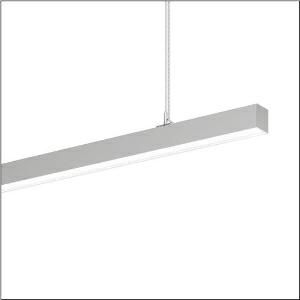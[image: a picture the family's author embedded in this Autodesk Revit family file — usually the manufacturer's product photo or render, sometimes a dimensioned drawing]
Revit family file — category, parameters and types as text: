
# Revit family: silica_r__21_51mx33tat7s_6391
name_source: partatom
category: Lighting Fixtures
units: mm (PartAtom-declared; Revit-internal decimal feet)

## family parameters
Cut with Voids When Loaded = No
Host = Face
Light Source = No
Part Type = Normal
Room Calculation Point = No
Round Connector Dimension = Use Diameter
Shared = No

## types (1)
- --- (1 x LED, 5740 lm, 53.8 W, 6500K)
    Apparent Load = 54 VA
    CIE Flux Codes = 78 96 99 56 100
    Color Rendering = 80
    Color Temperature = 6500K
    Default Elevation = 1800 mm
    Description = Silica® 21, office luminaire, primary optical cover: prismatic diffuser, of PMMA, CAT 2 (L<= 3000cd/m²), light emission: direct/indirect distribution, primary light characteristic: symmetric, installation type: suspended mounting, LED, rated luminous flux: 5.740lm, luminous efficacy: 102lm/W, light colour: 8tw, colour temperature: 2700..6500K, control gear: ECG DALI, with terminal, 3+2-pole, max. 2.5mm², mains connection: 220..240V, AC, 50/60Hz, rated input power: 56.5W, luminaire housing, of aluminium, metallic grey (RAL 9006), length: 1.204mm, width: 53mm, height: 53mm, protection rating (complete): IP20, insulation class (complete): insulation class I (protective earthing), certification: CE, permissible operating ambient temperature: 0..+35°C, standard: EN 50419, packaging unit: 1 piece
    Height = 53 mm
    Lamp = 1 x LED
    Lamp Light Flux = 5740 lm
    Lamp Power = 53.8 W
    Lamp count = 1
    Length = 1204 mm
    Luminous efficacy = 107 lm/W
    Manufacturer = Siteco
    ModVariant = No
    Model = 51MX33TAT7S
    Mounting Place = Ceiling
    Mounting Type = Pendant
    Number of Poles = 1
    OnlyDefault = Yes
    Power Factor = 1
    Product Name = Silica® 21
    Product group = office luminaire | ceiling pendant
    ProductGroupID = 902
    Protection Class = Protection class I
    Protection Degree = IP 20
    RLX_Detail_Level = 1
    RLX_Emergency_Light_Flux = 0 lm
    RLX_Emergency_Type = 0
    RLX_Emergency_Type_DB = No
    RlxData = <blob elided: 20189 chars, md5=af072bba>
    Socket = socket
    Standby Power = 0 W
    System Light Flux = 5740 lm
    System Power = 54 W
    Type Comments = individual setting
    Type Image = l_1313621.jpg
    URL = http://relux.com
    VarID = @adj_089115
    Voltage = 0 V
    Weight = 0.00 kg
    Width = 53 mm

## geometry (parser evidence)
native form markers: Blend x4, Sweep x14
no freeform markers — native parametric forms only
